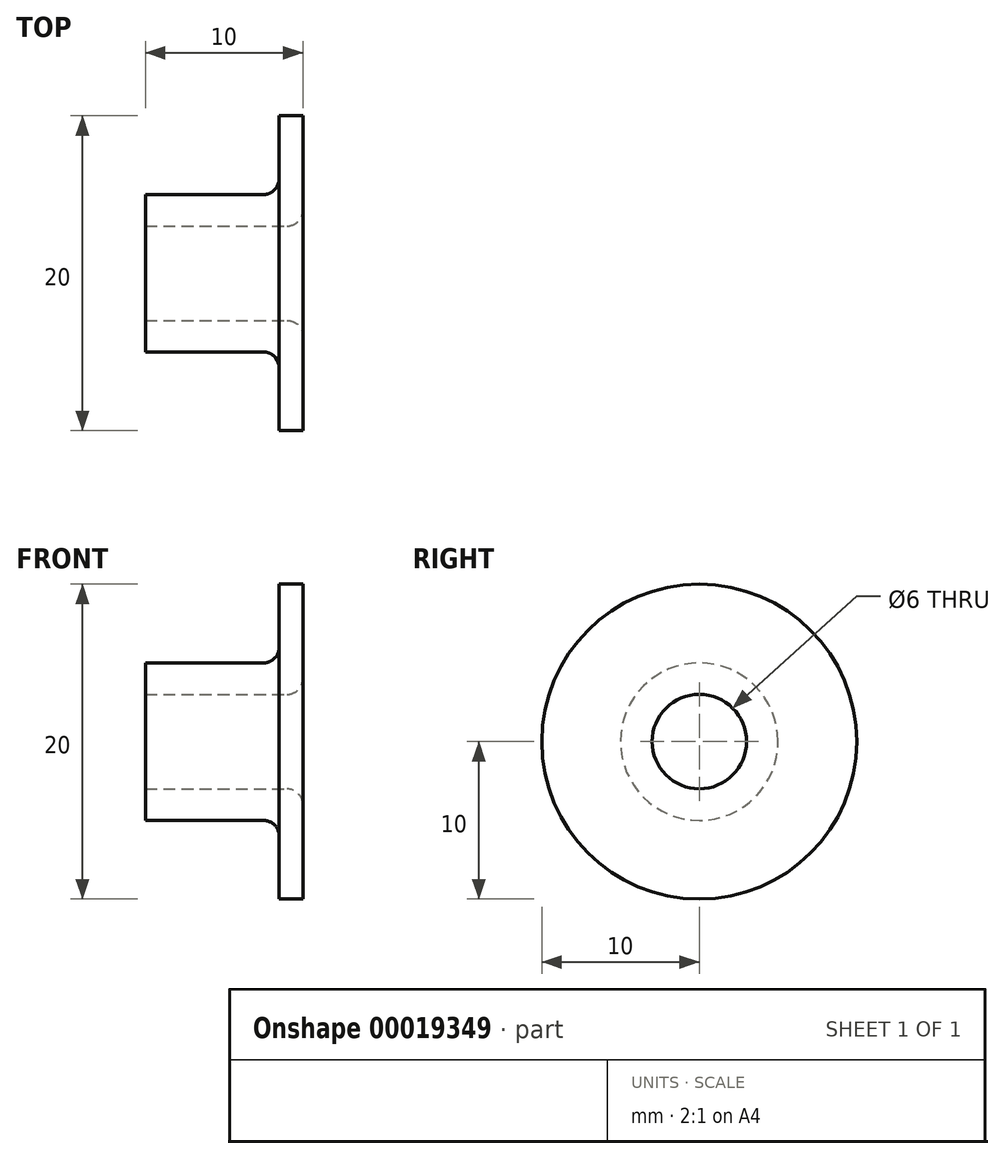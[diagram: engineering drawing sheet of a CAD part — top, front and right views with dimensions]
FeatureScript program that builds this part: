
annotation { "Feature Type Name" : "Feature", "Feature Type Description" : "" }
export const myFeature = defineFeature(function(context is Context, id is Id, definition is map)
    precondition{}
    {
        {
            var Q0;
            Q0=qCreatedBy(makeId("Right.planeOp"),FACE);
            var sketch = newSketch(context, id + "F0", { "sketchPlane" : qUnion([Q0])});
            skLineSegment(sketch, "E0", {"start": v(0, 0) * mm, "end": v(0, -10) * mm, "construction": true});
            skLineSegment(sketch, "E1", {"start": v(-10, 0) * mm, "end": v(-4, 0) * mm});
            skArc(sketch, "E2", {"start": v(-4, 0) * mm, "mid": v(-3.3, -0.3) * mm, "end": v(-3, -1) * mm});
            skLineSegment(sketch, "E3", {"start": v(-3, -1) * mm, "end": v(-3, -10) * mm});
            skLineSegment(sketch, "E4", {"start": v(-10, 0) * mm, "end": v(-10, -1.5) * mm});
            skLineSegment(sketch, "E5", {"start": v(-10, -1.5) * mm, "end": v(-6, -1.5) * mm});
            skArc(sketch, "E6", {"start": v(-6, -1.5) * mm, "mid": v(-5.3, -1.8) * mm, "end": v(-5, -2.5) * mm});
            skLineSegment(sketch, "E7", {"start": v(-5, -2.5) * mm, "end": v(-5, -10) * mm});
            skLineSegment(sketch, "E8", {"start": v(-5, -10) * mm, "end": v(-3, -10) * mm});
            skSolve(sketch);
        }
        {
            var Q0;
            Q0 = qSketchRegion(id + "F0", true);
            var Q1;
            Q1=sQuery(id+"F0.wireOp",EDGE,"E0");
            revolve(context, id + "F1", {"entities" : qUnion([Q0]), "axis" : qUnion([Q1]), "revolveType" : RevolveType.FULL});
        }
        {
            var Q0;
            Q0=makeQuery(id+"F1.opRevolve","SWEPT_BODY",BODY,{"disambiguationData":[OSD([sQuery(id+"F0.wireOp",EDGE,"E1"),sQuery(id+"F0.wireOp",EDGE,"E2"),sQuery(id+"F0.wireOp",EDGE,"E3"),sQuery(id+"F0.wireOp",EDGE,"E4"),sQuery(id+"F0.wireOp",EDGE,"E5"),sQuery(id+"F0.wireOp",EDGE,"E6"),sQuery(id+"F0.wireOp",EDGE,"E7"),sQuery(id+"F0.wireOp",EDGE,"E8")])]});
            transform(context, id + "F2", {"entities" : qUnion([Q0]), "transformType" : TransformType.TRANSLATION_3D, "dx" : 100 * mm, "dy" : 50 * mm, "dz" : 250 * mm, "makeCopy" : false});
        }
        {
            var Q0;
            Q0=makeQuery(id+"F1.opRevolve","SWEPT_FACE",FACE,{"disambiguationData":[OSD([sQuery(id+"F0.wireOp",EDGE,"E1")])]});
            var sketch = newSketch(context, id + "F3", { "sketchPlane" : qUnion([Q0])});
            skLineSegment(sketch, "E9", {"start": v(100, 60) * mm, "end": v(100, 40) * mm, "construction": true});
            skLineSegment(sketch, "E10", {"start": v(90, 50) * mm, "end": v(110, 50) * mm, "construction": true});
            skPoint(sketch, "E11", {"position": v(100, 50) * mm});
            skSolve(sketch);
        }
        {
            var Q0;
            Q0=makeQuery(id+"F1.opRevolve","SWEPT_BODY",BODY,{"disambiguationData":[OSD([sQuery(id+"F0.wireOp",EDGE,"E1"),sQuery(id+"F0.wireOp",EDGE,"E2"),sQuery(id+"F0.wireOp",EDGE,"E3"),sQuery(id+"F0.wireOp",EDGE,"E4"),sQuery(id+"F0.wireOp",EDGE,"E5"),sQuery(id+"F0.wireOp",EDGE,"E6"),sQuery(id+"F0.wireOp",EDGE,"E7"),sQuery(id+"F0.wireOp",EDGE,"E8")])]});
            var Q1;
            Q1=sQuery(id+"F3.wireOp",EDGE,"E9");
            transform(context, id + "F4", {"entities" : qUnion([Q0]), "transformType" : TransformType.ROTATION, "transformAxis" : qUnion([Q1]), "angle" : 270 * degree, "makeCopy" : false});
        }
    });
